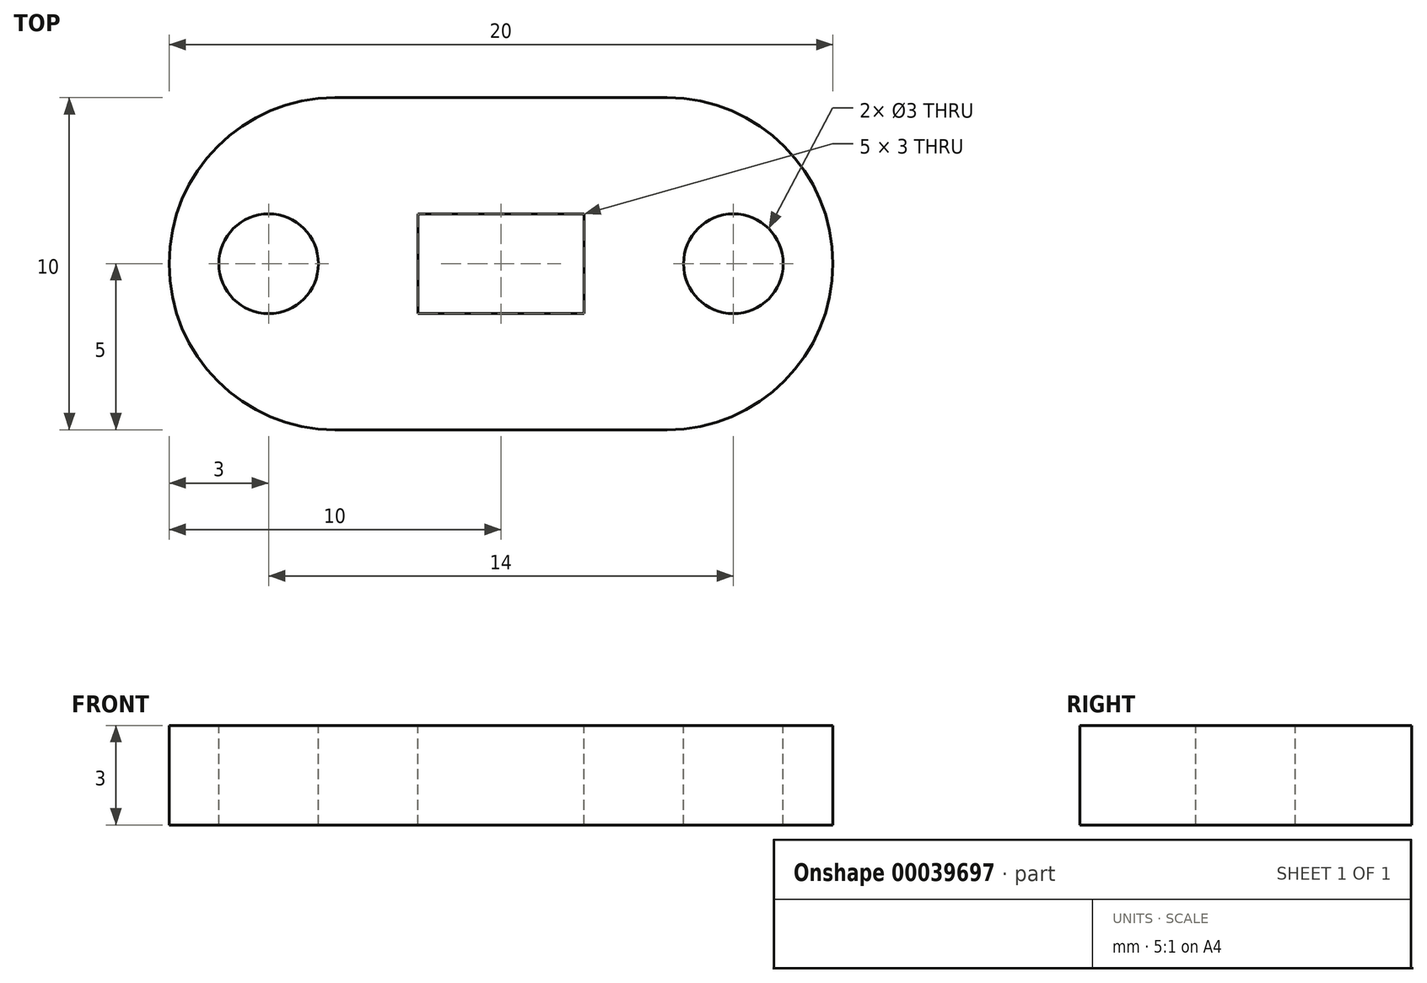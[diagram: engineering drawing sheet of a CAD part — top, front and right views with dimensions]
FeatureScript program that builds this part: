
annotation { "Feature Type Name" : "Feature", "Feature Type Description" : "" }
export const myFeature = defineFeature(function(context is Context, id is Id, definition is map)
    precondition{}
    {
        {
            var Q0;
            Q0=qCreatedBy(makeId("Top.planeOp"),FACE);
            var sketch = newSketch(context, id + "F0", { "sketchPlane" : qUnion([Q0])});
            skLineSegment(sketch, "E0.bottom", {"start": v(-10, 5) * mm, "end": v(10, 5) * mm});
            skLineSegment(sketch, "E0.top", {"start": v(-10, -5) * mm, "end": v(10, -5) * mm});
            skLineSegment(sketch, "E0.left", {"start": v(-10, 5) * mm, "end": v(-10, -5) * mm});
            skLineSegment(sketch, "E0.right", {"start": v(10, 5) * mm, "end": v(10, -5) * mm});
            skLineSegment(sketch, "E1.bottom", {"start": v(-2.5, 1.5) * mm, "end": v(2.5, 1.5) * mm});
            skLineSegment(sketch, "E1.top", {"start": v(-2.5, -1.5) * mm, "end": v(2.5, -1.5) * mm});
            skLineSegment(sketch, "E1.left", {"start": v(-2.5, 1.5) * mm, "end": v(-2.5, -1.5) * mm});
            skLineSegment(sketch, "E1.right", {"start": v(2.5, 1.5) * mm, "end": v(2.5, -1.5) * mm});
            skSolve(sketch);
        }
        {
            var Q0;
            Q0=makeQuery(id+"F0.imprint","IMPRINT",FACE,{"disambiguationData":[TD([[makeQuery(id+"F0.imprint","IMPRINT",EDGE,{"derivedFrom":sQuery(id+"F0.wireOp",EDGE,"E0.bottom")}),-1.0]])]});
            extrude(context, id + "F1", {"entities" : qUnion([Q0]), "oppositeDirection" : true, "depth" : 3 * mm});
        }
        {
            var Q0;
            Q0=makeQuery(id+"F1.opExtrude","SWEPT_EDGE",EDGE,{"disambiguationData":[OSD([sQuery(id+"F0.wireOp",EDGE,"E0.top"),sQuery(id+"F0.wireOp",EDGE,"E0.left")])]});
            var Q1;
            Q1=makeQuery(id+"F1.opExtrude","SWEPT_EDGE",EDGE,{"disambiguationData":[OSD([sQuery(id+"F0.wireOp",EDGE,"E0.bottom"),sQuery(id+"F0.wireOp",EDGE,"E0.left")])]});
            var Q2;
            Q2=makeQuery(id+"F1.opExtrude","SWEPT_EDGE",EDGE,{"disambiguationData":[OSD([sQuery(id+"F0.wireOp",EDGE,"E0.top"),sQuery(id+"F0.wireOp",EDGE,"E0.right")])]});
            var Q3;
            Q3=makeQuery(id+"F1.opExtrude","SWEPT_EDGE",EDGE,{"disambiguationData":[OSD([sQuery(id+"F0.wireOp",EDGE,"E0.bottom"),sQuery(id+"F0.wireOp",EDGE,"E0.right")])]});
            fillet(context, id + "F2", {"entities" : qUnion([Q0, Q1, Q2, Q3]), "radius" : 5 * mm, "tangentPropagation" : true, "allowEdgeOverflow" : false});
        }
        {
            var Q0;
            Q0=makeQuery(id+"F1.opExtrude","CAP_FACE",FACE,{"disambiguationData":[OSD([sQuery(id+"F0.wireOp",EDGE,"E0.bottom"),sQuery(id+"F0.wireOp",EDGE,"E0.top"),sQuery(id+"F0.wireOp",EDGE,"E0.left"),sQuery(id+"F0.wireOp",EDGE,"E0.right"),sQuery(id+"F0.wireOp",EDGE,"E1.bottom"),sQuery(id+"F0.wireOp",EDGE,"E1.top"),sQuery(id+"F0.wireOp",EDGE,"E1.left"),sQuery(id+"F0.wireOp",EDGE,"E1.right")])],"isStart":true});
            var sketch = newSketch(context, id + "F3", { "sketchPlane" : qUnion([Q0])});
            skPoint(sketch, "E2", {"position": v(-7, 0) * mm});
            skPoint(sketch, "E3.MirrorP", {"position": v(7, 0) * mm});
            skSolve(sketch);
        }
        {
            var Q0;
            Q0=sQuery(id+"F3.wireOp",VERTEX,"E2");
            var Q1;
            Q1=sQuery(id+"F3.wireOp",VERTEX,"E3.MirrorP");
            var Q2;
            Q2=makeQuery(id+"F1.opExtrude","SWEPT_BODY",BODY,{"disambiguationData":[OSD([sQuery(id+"F0.wireOp",EDGE,"E0.bottom"),sQuery(id+"F0.wireOp",EDGE,"E0.top"),sQuery(id+"F0.wireOp",EDGE,"E0.left"),sQuery(id+"F0.wireOp",EDGE,"E0.right"),sQuery(id+"F0.wireOp",EDGE,"E1.bottom"),sQuery(id+"F0.wireOp",EDGE,"E1.top"),sQuery(id+"F0.wireOp",EDGE,"E1.left"),sQuery(id+"F0.wireOp",EDGE,"E1.right")])]});
            hole(context, id + "F4", {"style" : HoleStyle.SIMPLE, "holeDiameter" : 3 * mm, "endStyle" : HoleEndStyle.THROUGH, "locations" : qUnion([Q0, Q1]), "scope" : qUnion([Q2])});
        }
    });
